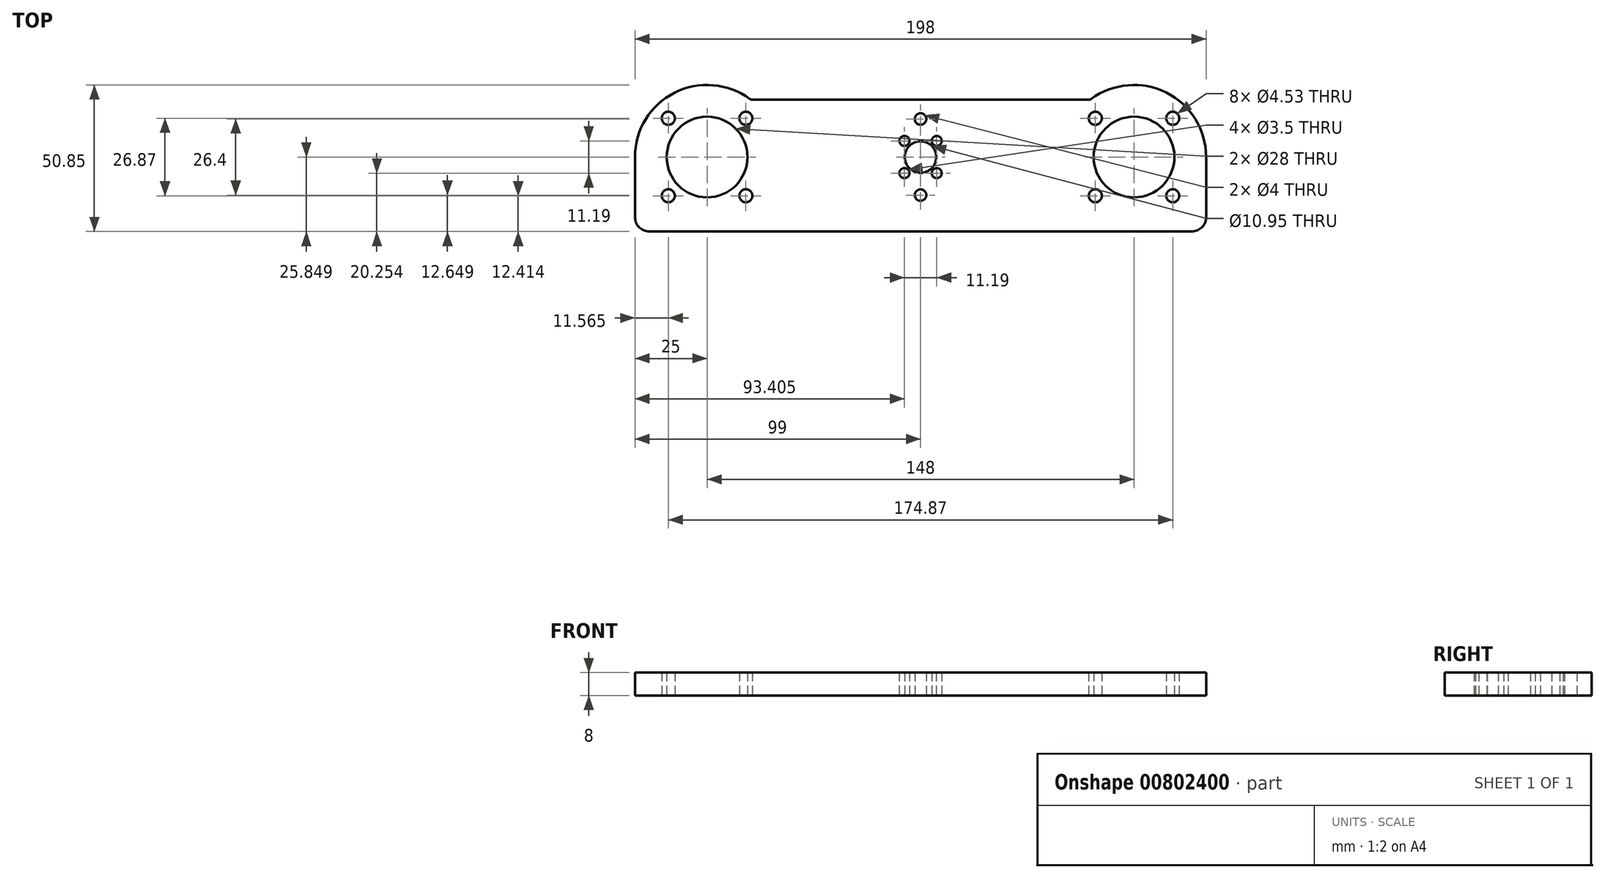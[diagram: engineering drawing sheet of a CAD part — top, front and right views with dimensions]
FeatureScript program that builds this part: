
annotation { "Feature Type Name" : "Feature", "Feature Type Description" : "" }
export const myFeature = defineFeature(function(context is Context, id is Id, definition is map)
    precondition{}
    {
        {
            var Q0;
            Q0=qCreatedBy(makeId("Top.planeOp"),FACE);
            var sketch = newSketch(context, id + "F0", { "sketchPlane" : qUnion([Q0])});
            skLineSegment(sketch, "E0", {"start": v(1.05, 1.5) * mm, "end": v(1.05, -48.27) * mm, "construction": true});
            skCircle(sketch, "E1", {"center": v(1.05, -18.42) * mm, "radius": 5.47 * mm});
            skLineSegment(sketch, "E2", {"start": v(-111.95, -18.42) * mm, "end": v(114.05, -18.42) * mm, "construction": true});
            skCircle(sketch, "E3", {"center": v(75.05, -18.42) * mm, "radius": 14 * mm});
            skLineSegment(sketch, "E4", {"start": v(114.05, -23.38) * mm, "end": v(-111.95, -23.38) * mm, "construction": true});
            skLineSegment(sketch, "E5", {"start": v(75.05, -18.42) * mm, "end": v(88.49, -31.86) * mm, "construction": true});
            skCircle(sketch, "E6", {"center": v(88.49, -31.86) * mm, "radius": 2.27 * mm});
            skCircle(sketch, "E7.1.0", {"center": v(88.49, -4.99) * mm, "radius": 2.27 * mm});
            skCircle(sketch, "E7.2.0", {"center": v(61.62, -4.99) * mm, "radius": 2.27 * mm});
            skCircle(sketch, "E7.3.0", {"center": v(61.62, -31.86) * mm, "radius": 2.27 * mm});
            skCircle(sketch, "E8.MirrorC", {"center": v(-72.95, -18.42) * mm, "radius": 14 * mm});
            skCircle(sketch, "E9.MirrorC", {"center": v(-86.38, -31.86) * mm, "radius": 2.27 * mm});
            skCircle(sketch, "E10.MirrorC", {"center": v(-59.51, -31.86) * mm, "radius": 2.27 * mm});
            skCircle(sketch, "E11.MirrorC", {"center": v(-59.51, -4.99) * mm, "radius": 2.27 * mm});
            skCircle(sketch, "E12.MirrorC", {"center": v(-86.38, -4.99) * mm, "radius": 2.27 * mm});
            skLineSegment(sketch, "E13", {"start": v(1.05, -18.42) * mm, "end": v(6.53, -18.42) * mm, "construction": true});
            skLineSegment(sketch, "E14", {"start": v(1.05, -18.42) * mm, "end": v(6.65, -24.02) * mm, "construction": true});
            skCircle(sketch, "E15", {"center": v(6.65, -24.02) * mm, "radius": 1.75 * mm});
            skCircle(sketch, "E16.1.0", {"center": v(6.65, -12.83) * mm, "radius": 1.75 * mm});
            skCircle(sketch, "E16.2.0", {"center": v(-4.54, -12.83) * mm, "radius": 1.75 * mm});
            skCircle(sketch, "E16.3.0", {"center": v(-4.54, -24.02) * mm, "radius": 1.75 * mm});
            skArc(sketch, "E17", {"start": v(-58.11, 1.7) * mm, "mid": v(-84.22, 3.9) * mm, "end": v(-97.95, -18.42) * mm});
            skLineSegment(sketch, "E18.trimOffspring", {"start": v(-57.52, 1.5) * mm, "end": v(59.62, 1.5) * mm});
            skLineSegment(sketch, "E19.trimOffspring", {"start": v(-84.72, -44.27) * mm, "end": v(86.82, -44.27) * mm});
            skPoint(sketch, "E20.visualSharp", {"position": v(-111.95, -69.27) * mm});
            skPoint(sketch, "E21.visualSharp", {"position": v(-95, -69.27) * mm});
            skPoint(sketch, "E22.visualSharp", {"position": v(-85.4, -44.27) * mm});
            skPoint(sketch, "E23.visualSharp", {"position": v(87.5, -44.27) * mm});
            skPoint(sketch, "E24.visualSharp", {"position": v(97.1, -69.27) * mm});
            skPoint(sketch, "E25.visualSharp", {"position": v(90.15, 1.5) * mm});
            skPoint(sketch, "E26.visualSharp", {"position": v(59.95, 1.5) * mm});
            skArc(sketch, "E26.filletArc", {"start": v(59.62, 1.5) * mm, "mid": v(59.93, 1.55) * mm, "end": v(60.21, 1.7) * mm});
            skPoint(sketch, "E27.visualSharp", {"position": v(-57.85, 1.5) * mm});
            skArc(sketch, "E27.filletArc", {"start": v(-58.11, 1.7) * mm, "mid": v(-57.83, 1.55) * mm, "end": v(-57.52, 1.5) * mm});
            skPoint(sketch, "E28.visualSharp", {"position": v(-88.05, 1.5) * mm});
            skLineSegment(sketch, "E29", {"start": v(-84.72, -44.27) * mm, "end": v(-92.95, -44.27) * mm});
            skCircle(sketch, "E30", {"center": v(1.05, -5.22) * mm, "radius": 2 * mm});
            skCircle(sketch, "E31", {"center": v(1.05, -31.62) * mm, "radius": 2 * mm});
            skLineSegment(sketch, "E32", {"start": v(-97.95, -18.42) * mm, "end": v(-97.95, -39.27) * mm});
            skArc(sketch, "E33.filletArc", {"start": v(-97.95, -39.27) * mm, "mid": v(-96.49, -42.8) * mm, "end": v(-92.95, -44.27) * mm});
            skArc(sketch, "E34.MirrorCS", {"start": v(60.21, 1.7) * mm, "mid": v(86.32, 3.9) * mm, "end": v(100.05, -18.42) * mm});
            skLineSegment(sketch, "E35.MirrorCS", {"start": v(100.05, -18.42) * mm, "end": v(100.05, -39.27) * mm});
            skArc(sketch, "E36.MirrorCS", {"start": v(100.05, -39.27) * mm, "mid": v(98.59, -42.8) * mm, "end": v(95.05, -44.27) * mm});
            skLineSegment(sketch, "E37", {"start": v(86.82, -44.27) * mm, "end": v(95.05, -44.27) * mm});
            skCircle(sketch, "E38", {"center": v(-86.38, -31.86) * mm, "radius": 4 * mm, "construction": true});
            skSolve(sketch);
        }
        {
            var Q0;
            Q0=makeQuery(id+"F0.imprint","IMPRINT",FACE,{"disambiguationData":[TD([[makeQuery(id+"F0.imprint","IMPRINT",EDGE,{"derivedFrom":sQuery(id+"F0.wireOp",EDGE,"E1")}),-1.0]])]});
            extrude(context, id + "F1", {"entities" : qUnion([Q0]), "depth" : 8 * mm, "offsetDistance" : 25 * mm});
        }
    });
